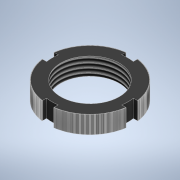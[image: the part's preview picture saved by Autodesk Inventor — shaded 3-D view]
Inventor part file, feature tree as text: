
AUTODESK INVENTOR PART (.ipt)
format: ipt  version: 2022 (Build 260153000, 153)  size: 1,364,992 bytes
history: native  units: mm
features: extrude x3, sketch x3, pattern_circular x1, thread x1
ambient origin geometry x8: Origin, YZ Plane, XZ Plane, XY Plane, X Axis, Y Axis, Z Axis, Center Point
bodies: Solid1 (feature_tree)
feature tree (8):
  extrude  "Extrusion1"  Depth=29.0mm
  sketch  "Sketch2"  dims[d2=6.0mm d3=0.0mm d4=2.0mm]
  extrude  "Extrusion3"  Depth=6.0mm
  pattern_circular  "Circular Pattern1"  [2 undecoded]
  extrude  "Extrusion4"  Depth=6.0mm
  thread  "Thread1"  [1 undecoded]
  sketch  "Sketch1"  dims[d0=20.0mm d1=29.0mm]
  sketch  "Sketch3"  dims[d5=2.0mm d6=2.0mm d7=2.0mm d8=1.5mm d13=0.1mm d14=0.1mm d15=6.0mm d16=0.0mm d17=14.35mm d19=0.15mm d20=3000.0mm d21=360.0deg d23=6.0mm d24=0.0mm d25=8.5mm d26=0.0mm]
note: 3 required parameter values undecoded (feature->parameter linkage not recoverable at this tier; creation-order binding heuristic only, values carry confidence <= 0.55)
